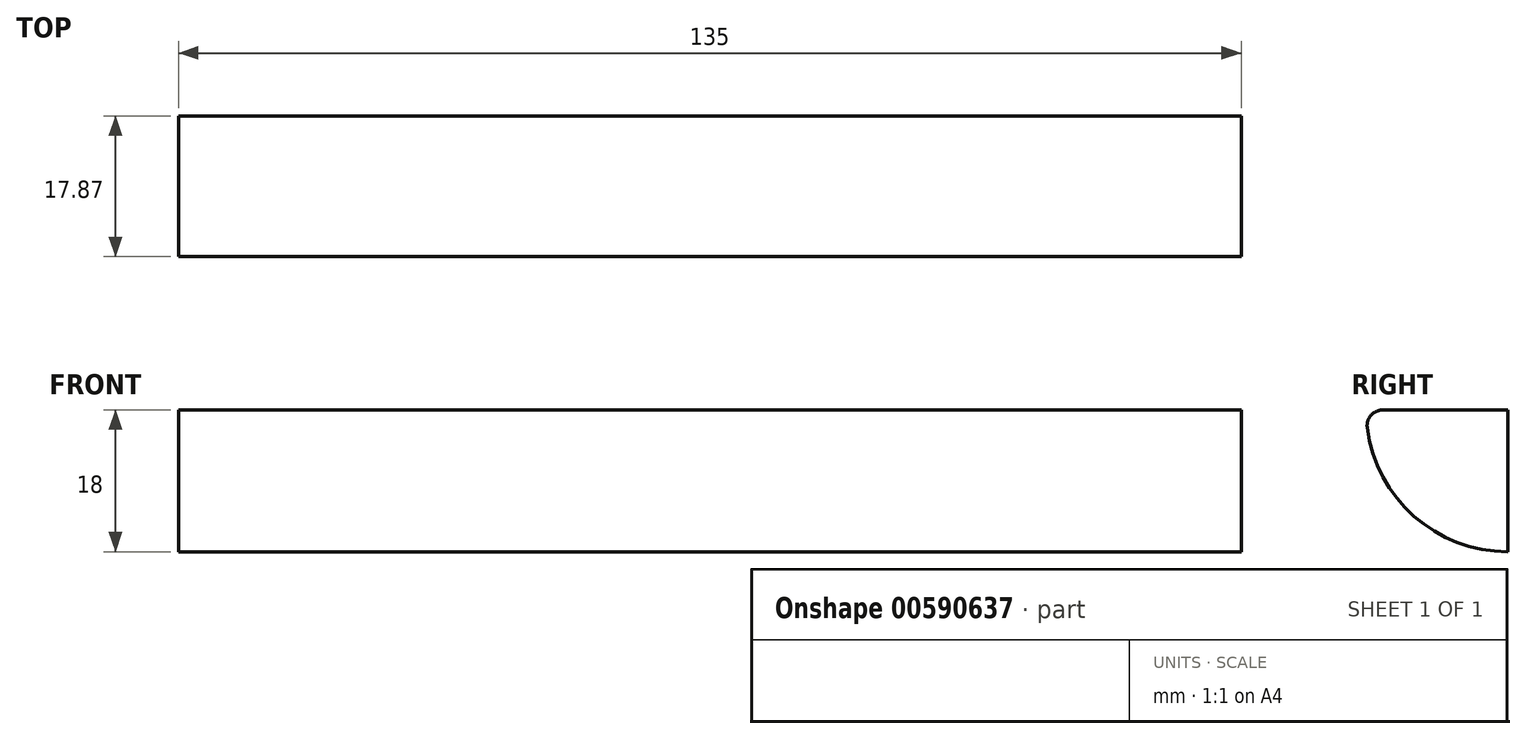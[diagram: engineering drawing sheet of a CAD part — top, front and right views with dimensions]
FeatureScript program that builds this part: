
annotation { "Feature Type Name" : "Feature", "Feature Type Description" : "" }
export const myFeature = defineFeature(function(context is Context, id is Id, definition is map)
    precondition{}
    {
        {
            var Q0;
            Q0=qCreatedBy(makeId("Right.planeOp"),FACE);
            var sketch = newSketch(context, id + "F0", { "sketchPlane" : qUnion([Q0])});
            skLineSegment(sketch, "E0.bottom", {"start": v(0, 0) * mm, "end": v(0, 0) * mm});
            skLineSegment(sketch, "E0.top", {"start": v(0, 18) * mm, "end": v(-15.87, 18) * mm});
            skLineSegment(sketch, "E0.left", {"start": v(0, 0) * mm, "end": v(0, 18) * mm});
            skLineSegment(sketch, "E0.right", {"start": v(-18, 18) * mm, "end": v(-18, 18) * mm});
            skPoint(sketch, "E1.visualSharp", {"position": v(-18, 0) * mm});
            skArc(sketch, "E1.filletArc", {"start": v(-17.86, 15.75) * mm, "mid": v(-11.9, 4.5) * mm, "end": v(0, 0) * mm});
            skPoint(sketch, "E2.visualSharp", {"position": v(-18, 18) * mm});
            skArc(sketch, "E2.filletArc", {"start": v(-15.87, 18) * mm, "mid": v(-17.37, 17.32) * mm, "end": v(-17.86, 15.75) * mm});
            skSolve(sketch);
        }
        {
            var Q0;
            Q0=makeQuery(id+"F0.imprint","IMPRINT",FACE,{"disambiguationData":[TD([[makeQuery(id+"F0.imprint","IMPRINT",EDGE,{"derivedFrom":sQuery(id+"F0.wireOp",EDGE,"E0.top")}),1.0]])]});
            extrude(context, id + "F1", {"entities" : qUnion([Q0]), "depth" : 135 * mm, "offsetDistance" : 25 * mm});
        }
    });
